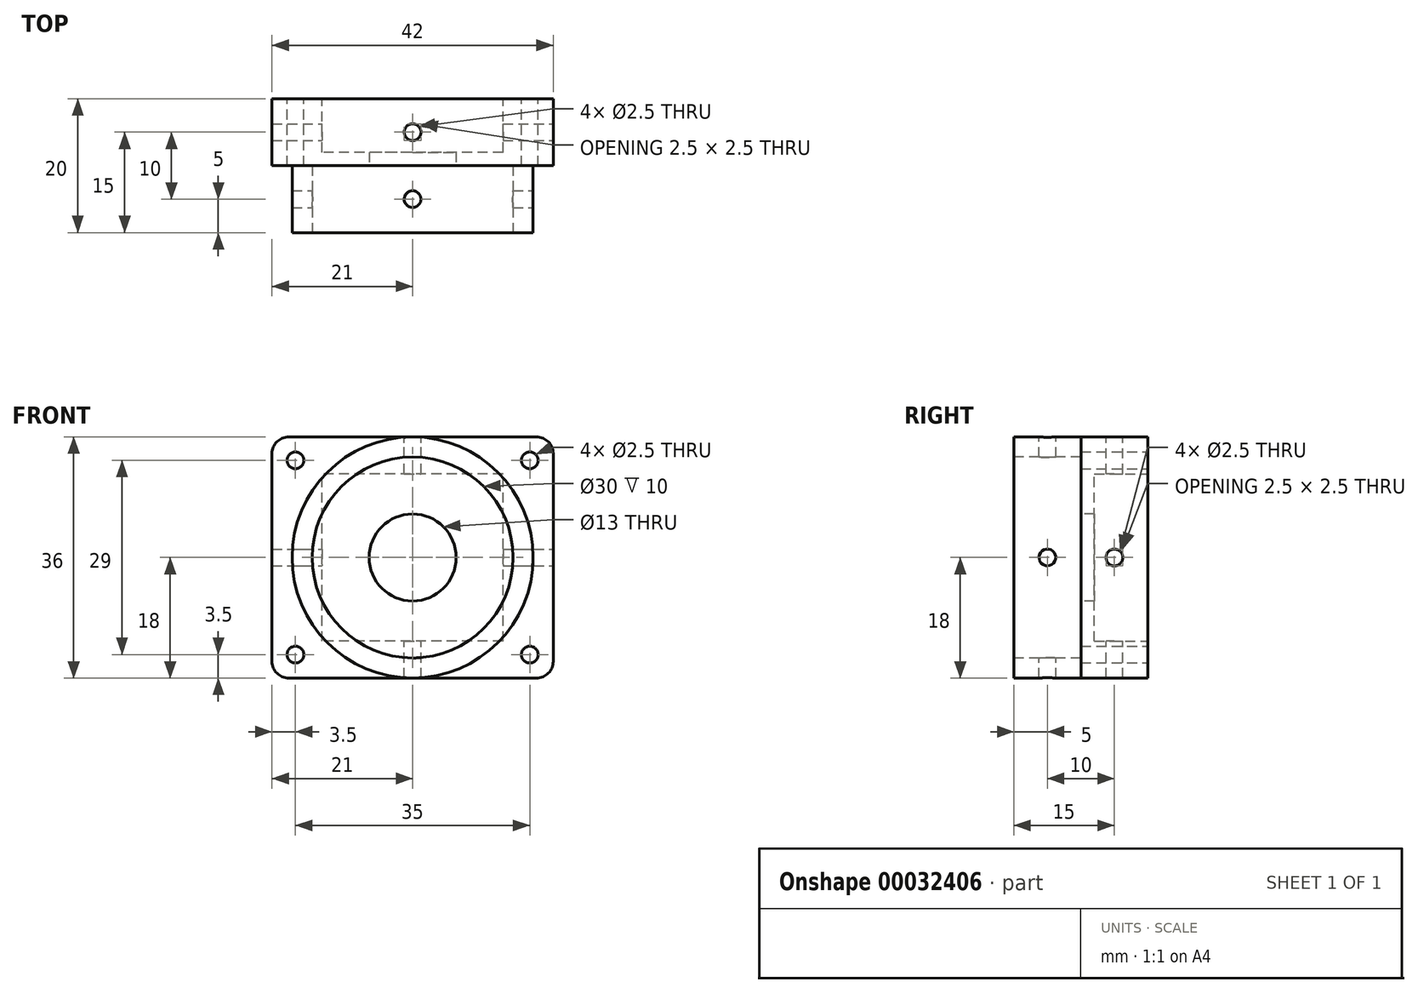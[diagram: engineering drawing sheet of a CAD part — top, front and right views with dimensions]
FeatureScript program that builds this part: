
annotation { "Feature Type Name" : "Feature", "Feature Type Description" : "" }
export const myFeature = defineFeature(function(context is Context, id is Id, definition is map)
    precondition{}
    {
        {
            var Q0;
            Q0=qCreatedBy(makeId("Front.planeOp"),FACE);
            var sketch = newSketch(context, id + "F0", { "sketchPlane" : qUnion([Q0])});
            skLineSegment(sketch, "E0.rect.bottom", {"start": v(18.5, -18) * mm, "end": v(-18.5, -18) * mm});
            skLineSegment(sketch, "E0.rect.top", {"start": v(18.5, 18) * mm, "end": v(-18.5, 18) * mm});
            skLineSegment(sketch, "E0.rect.left", {"start": v(21, -15.5) * mm, "end": v(21, 15.5) * mm});
            skLineSegment(sketch, "E0.rect.right", {"start": v(-21, -15.5) * mm, "end": v(-21, 15.5) * mm});
            skPoint(sketch, "E0.rect.middle", {"position": v(0, 0) * mm});
            skPoint(sketch, "E1.visualSharp", {"position": v(-21, 18) * mm});
            skArc(sketch, "E1.filletArc", {"start": v(-18.5, 18) * mm, "mid": v(-20.27, 17.27) * mm, "end": v(-21, 15.5) * mm});
            skPoint(sketch, "E2.visualSharp", {"position": v(-21, -18) * mm});
            skArc(sketch, "E2.filletArc", {"start": v(-21, -15.5) * mm, "mid": v(-20.27, -17.27) * mm, "end": v(-18.5, -18) * mm});
            skPoint(sketch, "E3.visualSharp", {"position": v(21, 18) * mm});
            skArc(sketch, "E3.filletArc", {"start": v(21, 15.5) * mm, "mid": v(20.27, 17.27) * mm, "end": v(18.5, 18) * mm});
            skPoint(sketch, "E4.visualSharp", {"position": v(21, -18) * mm});
            skArc(sketch, "E4.filletArc", {"start": v(18.5, -18) * mm, "mid": v(20.27, -17.27) * mm, "end": v(21, -15.5) * mm});
            skSolve(sketch);
        }
        {
            var Q0;
            Q0 = qSketchRegion(id + "F0", true);
            extrude(context, id + "F1", {"entities" : qUnion([Q0]), "oppositeDirection" : true, "depth" : 10 * mm});
        }
        {
            var Q0;
            Q0=makeQuery(id+"F1.opExtrude","CAP_FACE",FACE,{"disambiguationData":[OSD([sQuery(id+"F0.wireOp",EDGE,"E0.rect.bottom"),sQuery(id+"F0.wireOp",EDGE,"E0.rect.top"),sQuery(id+"F0.wireOp",EDGE,"E0.rect.left"),sQuery(id+"F0.wireOp",EDGE,"E0.rect.right")])],"isStart":true});
            var sketch = newSketch(context, id + "F2", { "sketchPlane" : qUnion([Q0])});
            skLineSegment(sketch, "E5.rect.bottom", {"start": v(-18.5, -18) * mm, "end": v(18.5, -18) * mm});
            skLineSegment(sketch, "E5.rect.top", {"start": v(-18.5, 18) * mm, "end": v(18.5, 18) * mm});
            skLineSegment(sketch, "E5.rect.left", {"start": v(18.5, -18) * mm, "end": v(18.5, 18) * mm});
            skLineSegment(sketch, "E5.rect.right", {"start": v(-18.5, -18) * mm, "end": v(-18.5, 18) * mm});
            skPoint(sketch, "E5.rect.middle", {"position": v(0, 0) * mm});
            skSolve(sketch);
        }
        {
            var Q0;
            Q0 = qSketchRegion(id + "F2", true);
            extrude(context, id + "F3", {"entities" : qUnion([Q0]), "operationType" : NewBodyOperationType.ADD, "depth" : 10 * mm});
        }
        {
            var Q0;
            Q0=makeQuery(id+"F1.opExtrude","CAP_FACE",FACE,{"disambiguationData":[OSD([sQuery(id+"F0.wireOp",EDGE,"E0.rect.bottom"),sQuery(id+"F0.wireOp",EDGE,"E0.rect.top"),sQuery(id+"F0.wireOp",EDGE,"E0.rect.left"),sQuery(id+"F0.wireOp",EDGE,"E0.rect.right")])],"isStart":false});
            var sketch = newSketch(context, id + "F4", { "sketchPlane" : qUnion([Q0])});
            skCircle(sketch, "E6", {"center": v(-17.5, 14.5) * mm, "radius": 1.25 * mm});
            skCircle(sketch, "E7.1.0.0", {"center": v(17.5, 14.5) * mm, "radius": 1.25 * mm});
            skLineSegment(sketch, "E7.direction1", {"start": v(-17.5, 14.5) * mm, "end": v(17.5, 14.5) * mm, "construction": true});
            skCircle(sketch, "E8", {"center": v(-17.5, -14.5) * mm, "radius": 1.25 * mm});
            skCircle(sketch, "E9", {"center": v(17.5, -14.5) * mm, "radius": 1.25 * mm});
            skSolve(sketch);
        }
        {
            var Q0;
            Q0 = qSketchRegion(id + "F4", true);
            extrude(context, id + "F5", {"entities" : qUnion([Q0]), "operationType" : NewBodyOperationType.REMOVE, "oppositeDirection" : true, "depth" : 25 * mm});
        }
        {
            var Q0;
            Q0=makeQuery(id+"F1.opExtrude","CAP_FACE",FACE,{"disambiguationData":[OSD([sQuery(id+"F0.wireOp",EDGE,"E0.rect.bottom"),sQuery(id+"F0.wireOp",EDGE,"E0.rect.top"),sQuery(id+"F0.wireOp",EDGE,"E0.rect.left"),sQuery(id+"F0.wireOp",EDGE,"E0.rect.right")])],"isStart":false});
            var sketch = newSketch(context, id + "F6", { "sketchPlane" : qUnion([Q0])});
            skLineSegment(sketch, "E10.rect.bottom", {"start": v(-13.5, -12.5) * mm, "end": v(13.5, -12.5) * mm});
            skLineSegment(sketch, "E10.rect.top", {"start": v(-13.5, 12.5) * mm, "end": v(13.5, 12.5) * mm});
            skLineSegment(sketch, "E10.rect.left", {"start": v(-13.5, -12.5) * mm, "end": v(-13.5, 12.5) * mm});
            skLineSegment(sketch, "E10.rect.right", {"start": v(13.5, -12.5) * mm, "end": v(13.5, 12.5) * mm});
            skPoint(sketch, "E10.rect.middle", {"position": v(0, 0) * mm});
            skSolve(sketch);
        }
        {
            var Q0;
            Q0 = qSketchRegion(id + "F6", true);
            extrude(context, id + "F7", {"entities" : qUnion([Q0]), "operationType" : NewBodyOperationType.REMOVE, "oppositeDirection" : true, "depth" : 8 * mm});
        }
        {
            var Q0;
            Q0=makeQuery(id+"F3.boolean.opBoolean","MERGE",FACE,{"derivedFrom":[makeQuery(id+"F1.opExtrude","SWEPT_FACE",FACE,{"disambiguationData":[OSD([sQuery(id+"F0.wireOp",EDGE,"E0.rect.top")])]}),makeQuery(id+"F3.opExtrude","SWEPT_FACE",FACE,{"disambiguationData":[OSD([sQuery(id+"F2.wireOp",EDGE,"E5.rect.top")])]})]});
            var sketch = newSketch(context, id + "F8", { "sketchPlane" : qUnion([Q0])});
            skCircle(sketch, "E11", {"center": v(0, 5) * mm, "radius": 1.25 * mm});
            skPoint(sketch, "E11.centerSnap0", {"position": v(0, 10) * mm});
            skCircle(sketch, "E12", {"center": v(0, -5) * mm, "radius": 1.25 * mm});
            skSolve(sketch);
        }
        {
            var Q0;
            Q0 = qSketchRegion(id + "F8", true);
            extrude(context, id + "F9", {"entities" : qUnion([Q0]), "operationType" : NewBodyOperationType.REMOVE, "endBound" : BoundingType.THROUGH_ALL, "oppositeDirection" : true, "depth" : 25 * mm});
        }
        {
            var Q0;
            Q0=makeQuery(id+"F1.opExtrude","SWEPT_FACE",FACE,{"disambiguationData":[OSD([sQuery(id+"F0.wireOp",EDGE,"E0.rect.left")])]});
            var sketch = newSketch(context, id + "F10", { "sketchPlane" : qUnion([Q0])});
            skCircle(sketch, "E13", {"center": v(5, 0) * mm, "radius": 1.25 * mm});
            skCircle(sketch, "E14", {"center": v(-5, 0) * mm, "radius": 1.25 * mm});
            skSolve(sketch);
        }
        {
            var Q0;
            Q0 = qSketchRegion(id + "F10", true);
            extrude(context, id + "F11", {"entities" : qUnion([Q0]), "operationType" : NewBodyOperationType.REMOVE, "endBound" : BoundingType.THROUGH_ALL, "oppositeDirection" : true, "depth" : 25 * mm});
        }
        {
            var Q0;
            Q0=makeQuery(id+"F3.opExtrude","CAP_FACE",FACE,{"disambiguationData":[OSD([sQuery(id+"F2.wireOp",EDGE,"E5.rect.bottom"),sQuery(id+"F2.wireOp",EDGE,"E5.rect.top"),sQuery(id+"F2.wireOp",EDGE,"E5.rect.left"),sQuery(id+"F2.wireOp",EDGE,"E5.rect.right")])],"isStart":false});
            var sketch = newSketch(context, id + "F12", { "sketchPlane" : qUnion([Q0])});
            skCircle(sketch, "E15", {"center": v(0, 0) * mm, "radius": 18 * mm});
            skSolve(sketch);
        }
        {
            var Q0;
            Q0=makeQuery(id+"F3.opExtrude","CAP_FACE",FACE,{"disambiguationData":[OSD([sQuery(id+"F2.wireOp",EDGE,"E5.rect.bottom"),sQuery(id+"F2.wireOp",EDGE,"E5.rect.top"),sQuery(id+"F2.wireOp",EDGE,"E5.rect.left"),sQuery(id+"F2.wireOp",EDGE,"E5.rect.right")])],"isStart":false});
            var sketch = newSketch(context, id + "F13", { "sketchPlane" : qUnion([Q0])});
            skCircle(sketch, "E16", {"center": v(0, 0) * mm, "radius": 15 * mm});
            skSolve(sketch);
        }
        {
            var Q0;
            Q0 = qSketchRegion(id + "F13", true);
            extrude(context, id + "F14", {"entities" : qUnion([Q0]), "operationType" : NewBodyOperationType.REMOVE, "oppositeDirection" : true, "depth" : 10 * mm});
        }
        {
            var Q0;
            {var subQ2=sQuery(id+"F12.wireOp",EDGE,"E15");var subQ8=sQuery(id+"F2.wireOp",EDGE,"E5.rect.bottom");var subQ11=makeQuery(id+"F3.opExtrude","CAP_EDGE",EDGE,{"disambiguationData":[OSD([subQ8])],"isStart":false});var subQ12=makeQuery(id+"F12.imprint","INTERSECT",VERTEX,{"derivedFrom":[subQ11,subQ2]});Q0=makeQuery(id+"F12.imprint","IMPRINT",FACE,{"disambiguationData":[TD([[makeQuery(id+"F12.imprint","IMPRINT",EDGE,{"disambiguationData":[TD([[subQ12,-1.0]])],"derivedFrom":subQ2}),-1.0]])]});}
            var Q1;
            {var subQ2=sQuery(id+"F12.wireOp",EDGE,"E15");var subQ8=sQuery(id+"F2.wireOp",EDGE,"E5.rect.bottom");var subQ11=makeQuery(id+"F3.opExtrude","CAP_EDGE",EDGE,{"disambiguationData":[OSD([subQ8])],"isStart":false});var subQ12=makeQuery(id+"F12.imprint","INTERSECT",VERTEX,{"derivedFrom":[subQ11,subQ2]});Q1=makeQuery(id+"F12.imprint","IMPRINT",FACE,{"disambiguationData":[TD([[makeQuery(id+"F12.imprint","IMPRINT",EDGE,{"disambiguationData":[TD([[subQ12,1.0]])],"derivedFrom":subQ2}),-1.0]])]});}
            extrude(context, id + "F15", {"entities" : qUnion([Q0, Q1]), "operationType" : NewBodyOperationType.REMOVE, "oppositeDirection" : true, "depth" : 10 * mm});
        }
        {
            var Q0;
            Q0=makeQuery(id+"F14.boolean.opBoolean","COPY",FACE,{"derivedFrom":makeQuery(id+"F14.opExtrude","CAP_FACE",FACE,{"disambiguationData":[OSD([sQuery(id+"F13.wireOp",EDGE,"E16")])],"isStart":false})});
            var sketch = newSketch(context, id + "F16", { "sketchPlane" : qUnion([Q0])});
            skCircle(sketch, "E17", {"center": v(0, 0) * mm, "radius": 6.5 * mm});
            skSolve(sketch);
        }
        {
            var Q0;
            Q0 = qSketchRegion(id + "F16", true);
            extrude(context, id + "F17", {"entities" : qUnion([Q0]), "operationType" : NewBodyOperationType.REMOVE, "endBound" : BoundingType.THROUGH_ALL, "oppositeDirection" : true, "depth" : 25 * mm});
        }
    });
